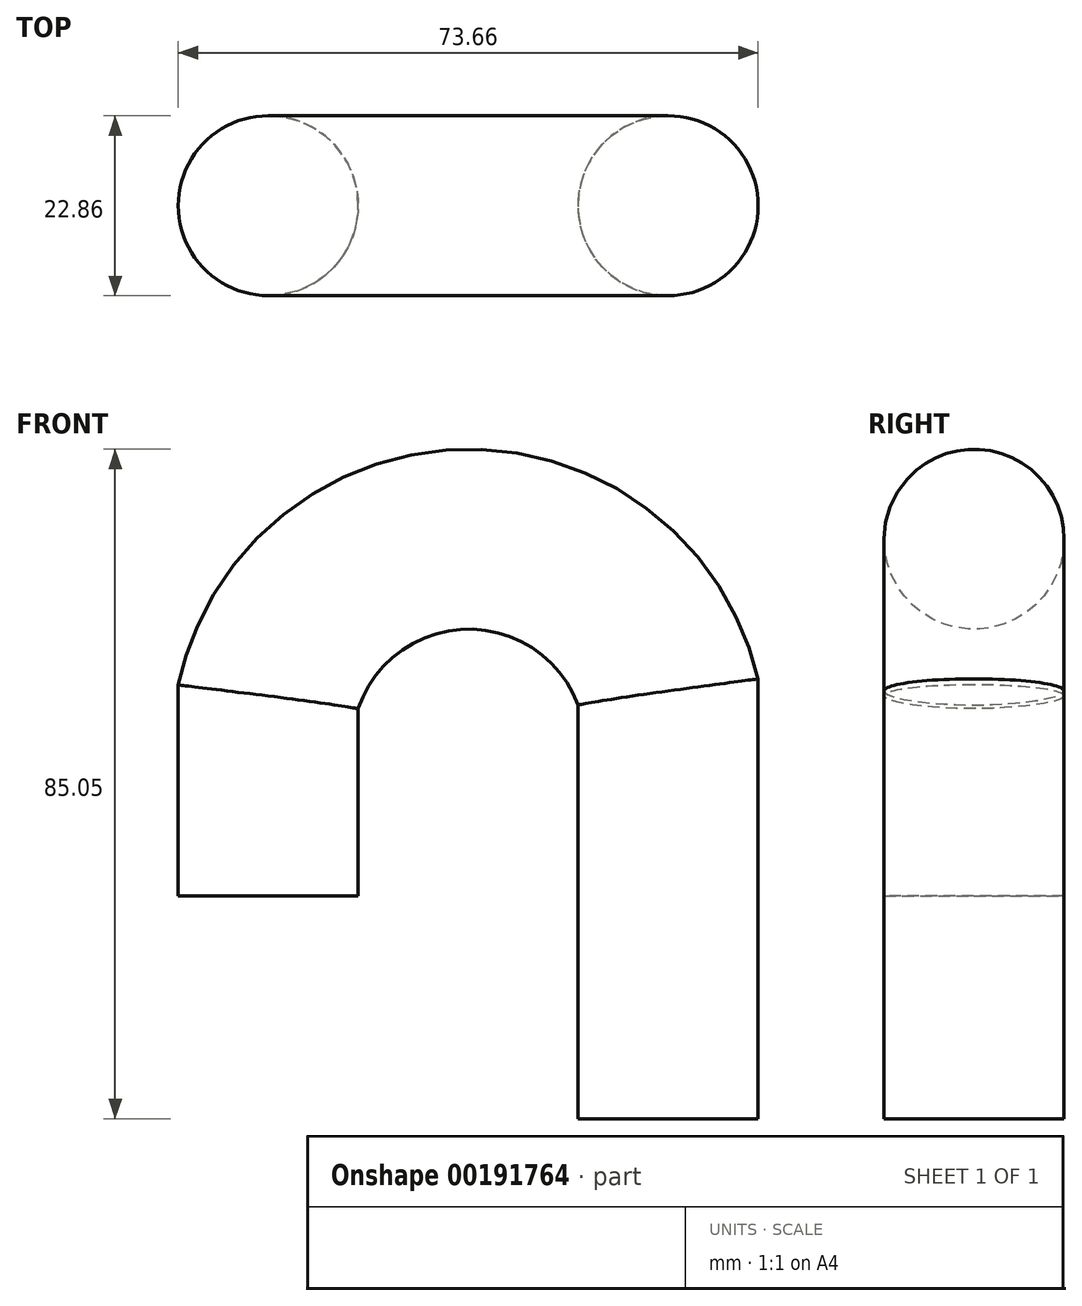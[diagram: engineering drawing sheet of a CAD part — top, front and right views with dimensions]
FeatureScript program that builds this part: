
annotation { "Feature Type Name" : "Feature", "Feature Type Description" : "" }
export const myFeature = defineFeature(function(context is Context, id is Id, definition is map)
    precondition{}
    {
        {
            var Q0;
            Q0=qCreatedBy(makeId("Front.planeOp"),FACE);
            var sketch = newSketch(context, id + "F0", { "sketchPlane" : qUnion([Q0])});
            skLineSegment(sketch, "E0", {"start": v(-29.23, 53.7) * mm, "end": v(-29.23, 28.3) * mm});
            skLineSegment(sketch, "E1", {"start": v(21.57, 54.33) * mm, "end": v(21.57, 0) * mm});
            skArc(sketch, "E2", {"start": v(21.57, 54.33) * mm, "mid": v(-4.07, 73.61) * mm, "end": v(-29.23, 53.7) * mm});
            skSolve(sketch);
        }
        {
            var Q0;
            Q0=qCreatedBy(makeId("Top.planeOp"),FACE);
            var sketch = newSketch(context, id + "F1", { "sketchPlane" : qUnion([Q0])});
            skCircle(sketch, "E3", {"center": v(21.57, 0) * mm, "radius": 11.43 * mm});
            skSolve(sketch);
        }
        {
            var Q0;
            Q0=makeQuery(id+"F1.imprint","IMPRINT",FACE,{"disambiguationData":[TD([[makeQuery(id+"F1.imprint","IMPRINT",EDGE,{"derivedFrom":sQuery(id+"F1.wireOp",EDGE,"E3")}),1.0]])]});
            var Q1;
            Q1 = qConstructionFilter(qBodyType(qCreatedBy(id + "F0" ,EDGE), BodyType.WIRE), ConstructionObject.NO);
            sweep(context, id + "F2", {"profiles" : qUnion([Q0]), "path" : qUnion([Q1])});
        }
    });
